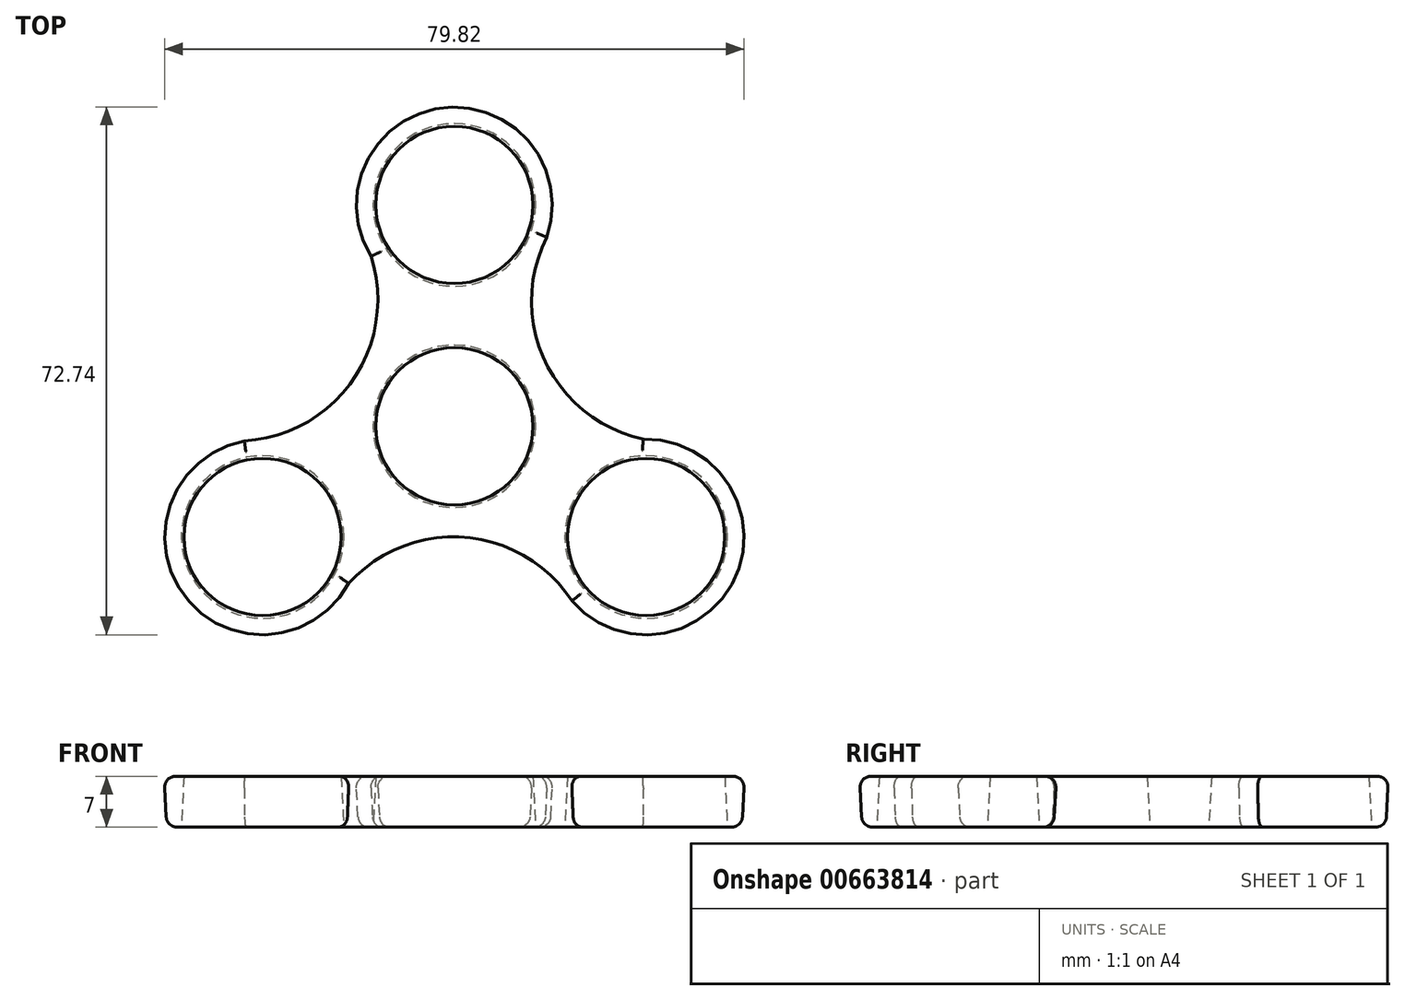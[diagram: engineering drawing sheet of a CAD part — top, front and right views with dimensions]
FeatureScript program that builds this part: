
annotation { "Feature Type Name" : "Feature", "Feature Type Description" : "" }
export const myFeature = defineFeature(function(context is Context, id is Id, definition is map)
    precondition{}
    {
        {
            var Q0;
            Q0=qCreatedBy(makeId("Top.planeOp"),FACE);
            var sketch = newSketch(context, id + "F0", { "sketchPlane" : qUnion([Q0])});
            skCircle(sketch, "E0", {"center": v(0, 0) * mm, "radius": 11.2 * mm});
            skCircle(sketch, "E1", {"center": v(0, 30.51) * mm, "radius": 11.2 * mm});
            skArc(sketch, "E2", {"start": v(11.63, 24.27) * mm, "mid": v(-0.41, 43.7) * mm, "end": v(-11.22, 23.56) * mm});
            skArc(sketch, "E3.1.0", {"start": v(-26.84, -2.06) * mm, "mid": v(-37.65, -22.21) * mm, "end": v(-14.8, -21.5) * mm});
            skCircle(sketch, "E3.1.1", {"center": v(-26.43, -15.26) * mm, "radius": 11.2 * mm});
            skArc(sketch, "E3.2.0", {"start": v(15.2, -22.2) * mm, "mid": v(38.06, -21.5) * mm, "end": v(26.01, -2.06) * mm});
            skCircle(sketch, "E3.2.1", {"center": v(26.43, -15.26) * mm, "radius": 11.2 * mm});
            skArc(sketch, "E4", {"start": v(12.46, 26.16) * mm, "mid": v(12.3, 8.72) * mm, "end": v(26.01, -2.06) * mm});
            skArc(sketch, "E5.1.0", {"start": v(-28.9, -2.29) * mm, "mid": v(-13.7, 6.3) * mm, "end": v(-11.22, 23.56) * mm});
            skArc(sketch, "E5.2.0", {"start": v(16.43, -23.87) * mm, "mid": v(1.4, -15) * mm, "end": v(-14.8, -21.5) * mm});
            skSolve(sketch);
        }
        {
            var Q0;
            Q0=makeQuery(id+"F0.imprint","IMPRINT",FACE,{"disambiguationData":[TD([[makeQuery(id+"F0.imprint","IMPRINT",EDGE,{"derivedFrom":sQuery(id+"F0.wireOp",EDGE,"E0")}),-1.0]])]});
            extrude(context, id + "F1", {"entities" : qUnion([Q0]), "depth" : 7 * mm, "offsetDistance" : 25 * mm, "hasDraft" : true, "draftAngle" : 3 * degree});
        }
        {
            var Q0;
            Q0=makeQuery(id+"F1.opExtrude","CAP_EDGE",EDGE,{"disambiguationData":[OSD([sQuery(id+"F0.wireOp",EDGE,"E4")])],"isStart":false});
            var Q1;
            Q1=makeQuery(id+"F1.opExtrude","CAP_EDGE",EDGE,{"disambiguationData":[OSD([sQuery(id+"F0.wireOp",EDGE,"E3.2.0")])],"isStart":false});
            var Q2;
            Q2=makeQuery(id+"F1.opExtrude","CAP_EDGE",EDGE,{"disambiguationData":[OSD([sQuery(id+"F0.wireOp",EDGE,"E5.2.0")])],"isStart":false});
            var Q3;
            Q3=makeQuery(id+"F1.opExtrude","CAP_EDGE",EDGE,{"disambiguationData":[OSD([sQuery(id+"F0.wireOp",EDGE,"E3.1.0")])],"isStart":false});
            var Q4;
            Q4=makeQuery(id+"F1.opExtrude","CAP_EDGE",EDGE,{"disambiguationData":[OSD([sQuery(id+"F0.wireOp",EDGE,"E5.1.0")])],"isStart":false});
            var Q5;
            Q5=makeQuery(id+"F1.opExtrude","CAP_EDGE",EDGE,{"disambiguationData":[OSD([sQuery(id+"F0.wireOp",EDGE,"E2")])],"isStart":false});
            fillet(context, id + "F2", {"entities" : qUnion([Q0, Q1, Q2, Q3, Q4, Q5]), "radius" : 1.5 * mm, "tangentPropagation" : true, "allowEdgeOverflow" : false});
        }
        {
            var Q0;
            Q0=makeQuery(id+"F1.opExtrude","CAP_EDGE",EDGE,{"disambiguationData":[OSD([sQuery(id+"F0.wireOp",EDGE,"E5.2.0")])],"isStart":true});
            var Q1;
            Q1=makeQuery(id+"F1.opExtrude","CAP_EDGE",EDGE,{"disambiguationData":[OSD([sQuery(id+"F0.wireOp",EDGE,"E3.1.0")])],"isStart":true});
            var Q2;
            Q2=makeQuery(id+"F1.opExtrude","CAP_EDGE",EDGE,{"disambiguationData":[OSD([sQuery(id+"F0.wireOp",EDGE,"E5.1.0")])],"isStart":true});
            var Q3;
            Q3=makeQuery(id+"F1.opExtrude","CAP_EDGE",EDGE,{"disambiguationData":[OSD([sQuery(id+"F0.wireOp",EDGE,"E2")])],"isStart":true});
            var Q4;
            Q4=makeQuery(id+"F1.opExtrude","CAP_EDGE",EDGE,{"disambiguationData":[OSD([sQuery(id+"F0.wireOp",EDGE,"E4")])],"isStart":true});
            var Q5;
            Q5=makeQuery(id+"F1.opExtrude","CAP_EDGE",EDGE,{"disambiguationData":[OSD([sQuery(id+"F0.wireOp",EDGE,"E3.2.0")])],"isStart":true});
            fillet(context, id + "F3", {"entities" : qUnion([Q0, Q1, Q2, Q3, Q4, Q5]), "radius" : 1.5 * mm, "tangentPropagation" : true, "allowEdgeOverflow" : false});
        }
    });
